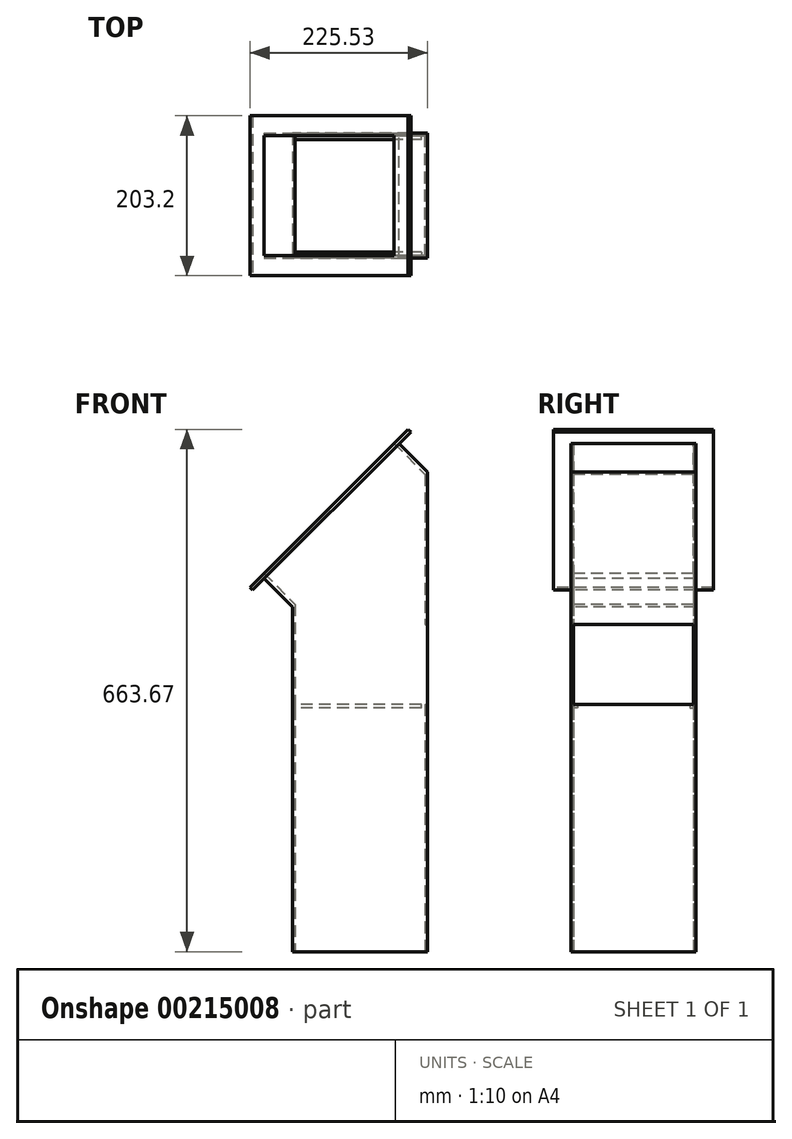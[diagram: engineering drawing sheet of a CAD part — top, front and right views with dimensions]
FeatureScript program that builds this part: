
annotation { "Feature Type Name" : "Feature", "Feature Type Description" : "" }
export const myFeature = defineFeature(function(context is Context, id is Id, definition is map)
    precondition{}
    {
        {
            var Q0;
            Q0=qCreatedBy(makeId("Top.planeOp"),FACE);
            var sketch = newSketch(context, id + "F0", { "sketchPlane" : qUnion([Q0])});
            skLineSegment(sketch, "E0.bottom", {"start": v(82.55, -76.2) * mm, "end": v(-82.55, -76.2) * mm});
            skLineSegment(sketch, "E0.top", {"start": v(82.55, 76.2) * mm, "end": v(-82.55, 76.2) * mm});
            skLineSegment(sketch, "E0.left", {"start": v(82.55, -76.2) * mm, "end": v(82.55, 76.2) * mm});
            skLineSegment(sketch, "E0.right", {"start": v(-82.55, -76.2) * mm, "end": v(-82.55, 76.2) * mm});
            skPoint(sketch, "E0.middle", {"position": v(0, 0) * mm});
            skLineSegment(sketch, "E1.0", {"start": v(-85.73, -79.38) * mm, "end": v(-85.73, 79.37) * mm});
            skLineSegment(sketch, "E1.1", {"start": v(85.73, -79.37) * mm, "end": v(-85.73, -79.38) * mm});
            skLineSegment(sketch, "E1.2", {"start": v(85.73, -79.37) * mm, "end": v(85.72, 79.38) * mm});
            skLineSegment(sketch, "E1.3", {"start": v(85.72, 79.38) * mm, "end": v(-85.73, 79.37) * mm});
            skSolve(sketch);
        }
        {
            var Q0;
            Q0 = qSketchRegion(id + "F0", true);
            extrude(context, id + "F1", {"entities" : qUnion([Q0]), "depth" : 609.6 * mm});
        }
        {
            var Q0;
            Q0=makeQuery(id+"F1.opExtrude","SWEPT_FACE",FACE,{"disambiguationData":[OSD([sQuery(id+"F0.wireOp",EDGE,"E1.1")])]});
            var sketch = newSketch(context, id + "F2", { "sketchPlane" : qUnion([Q0])});
            skLineSegment(sketch, "E2", {"start": v(85.72, 609.6) * mm, "end": v(-85.73, 609.6) * mm});
            skLineSegment(sketch, "E3", {"start": v(-85.73, 609.6) * mm, "end": v(-85.73, 438.15) * mm});
            skLineSegment(sketch, "E4", {"start": v(-85.73, 438.15) * mm, "end": v(85.72, 609.6) * mm});
            skSolve(sketch);
        }
        {
            var Q0;
            Q0 = qSketchRegion(id + "F2", true);
            extrude(context, id + "F3", {"entities" : qUnion([Q0]), "operationType" : NewBodyOperationType.REMOVE, "endBound" : BoundingType.THROUGH_ALL, "oppositeDirection" : true, "depth" : 25.4 * mm});
        }
        {
            var Q0;
            Q0=makeQuery(id+"F3.boolean.opBoolean","COPY",FACE,{"derivedFrom":makeQuery(id+"F3.opExtrude","SWEPT_FACE",FACE,{"disambiguationData":[OSD([sQuery(id+"F2.wireOp",EDGE,"E4")])]})});
            var sketch = newSketch(context, id + "F4", { "sketchPlane" : qUnion([Q0])});
            skLineSegment(sketch, "E5.0", {"start": v(-76.2, 253.7) * mm, "end": v(-76.2, 487.18) * mm});
            skLineSegment(sketch, "E6.0", {"start": v(-76.2, 487.18) * mm, "end": v(76.2, 487.18) * mm});
            skLineSegment(sketch, "E7.0", {"start": v(76.2, 253.7) * mm, "end": v(76.2, 487.18) * mm});
            skLineSegment(sketch, "E8.0", {"start": v(-76.2, 253.7) * mm, "end": v(76.2, 253.7) * mm});
            skLineSegment(sketch, "E9.0", {"start": v(-101.6, 228.3) * mm, "end": v(-101.6, 512.58) * mm});
            skLineSegment(sketch, "E9.1", {"start": v(-101.6, 228.3) * mm, "end": v(101.6, 228.3) * mm});
            skLineSegment(sketch, "E9.2", {"start": v(101.6, 228.3) * mm, "end": v(101.6, 512.58) * mm});
            skLineSegment(sketch, "E9.3", {"start": v(-101.6, 512.58) * mm, "end": v(101.6, 512.58) * mm});
            skSolve(sketch);
        }
        {
            var Q0;
            Q0 = qSketchRegion(id + "F4", true);
            extrude(context, id + "F5", {"entities" : qUnion([Q0]), "operationType" : NewBodyOperationType.ADD, "depth" : 55.56 * mm});
        }
        {
            var Q0;
            Q0=makeQuery(id+"F1.opExtrude","SWEPT_FACE",FACE,{"disambiguationData":[OSD([sQuery(id+"F0.wireOp",EDGE,"E1.2")])]});
            var sketch = newSketch(context, id + "F6", { "sketchPlane" : qUnion([Q0])});
            skLineSegment(sketch, "E10.0", {"start": v(76.2, 441.32) * mm, "end": v(-76.2, 441.32) * mm, "construction": true});
            skLineSegment(sketch, "E11.0", {"start": v(76.2, 415.93) * mm, "end": v(-76.2, 415.93) * mm});
            skLineSegment(sketch, "E12", {"start": v(-76.2, 415.93) * mm, "end": v(-76.2, 314.32) * mm});
            skLineSegment(sketch, "E13", {"start": v(-76.2, 314.32) * mm, "end": v(76.2, 314.32) * mm});
            skLineSegment(sketch, "E14", {"start": v(76.2, 314.32) * mm, "end": v(76.2, 415.93) * mm});
            skSolve(sketch);
        }
        {
            var Q0;
            Q0 = qSketchRegion(id + "F6", true);
            extrude(context, id + "F7", {"entities" : qUnion([Q0]), "operationType" : NewBodyOperationType.REMOVE, "oppositeDirection" : true, "depth" : 25.4 * mm});
        }
        {
            var Q0;
            Q0=makeQuery(id+"F7.boolean.opBoolean","MERGE",FACE,{"derivedFrom":[makeQuery(id+"F5.boolean.opBoolean","MERGE",FACE,{"derivedFrom":[makeQuery(id+"F1.opExtrude","SWEPT_FACE",FACE,{"disambiguationData":[OSD([sQuery(id+"F0.wireOp",EDGE,"E0.bottom")])]}),makeQuery(id+"F5.opExtrude","SWEPT_FACE",FACE,{"disambiguationData":[OSD([sQuery(id+"F4.wireOp",EDGE,"E7.0")])]})]}),makeQuery(id+"F7.opExtrude","SWEPT_FACE",FACE,{"disambiguationData":[OSD([sQuery(id+"F6.wireOp",EDGE,"E12")])]})]});
            var sketch = newSketch(context, id + "F8", { "sketchPlane" : qUnion([Q0])});
            skLineSegment(sketch, "E15.0", {"start": v(-82.55, 314.32) * mm, "end": v(-85.72, 314.32) * mm});
            skLineSegment(sketch, "E16.bottom", {"start": v(-82.55, 314.32) * mm, "end": v(82.55, 314.32) * mm});
            skLineSegment(sketch, "E16.top", {"start": v(-82.55, 309.56) * mm, "end": v(82.55, 309.56) * mm});
            skLineSegment(sketch, "E16.left", {"start": v(-82.55, 314.32) * mm, "end": v(-82.55, 309.56) * mm});
            skLineSegment(sketch, "E16.right", {"start": v(82.55, 314.32) * mm, "end": v(82.55, 309.56) * mm});
            skLineSegment(sketch, "E17", {"start": v(-77.79, 314.32) * mm, "end": v(-77.79, 309.56) * mm});
            skSolve(sketch);
        }
        {
            var Q0;
            {var subQ0=sQuery(id+"F8.wireOp",EDGE,"E16.right");Q0=makeQuery(id+"F8.imprint","IMPRINT",FACE,{"disambiguationData":[TD([[makeQuery(id+"F8.imprint","IMPRINT",EDGE,{"derivedFrom":subQ0}),-1.0]])]});}
            extrude(context, id + "F9", {"entities" : qUnion([Q0]), "operationType" : NewBodyOperationType.ADD, "depth" : 4.76 * mm});
        }
        {
            var Q0;
            Q0=makeQuery(id+"F7.boolean.opBoolean","MERGE",FACE,{"derivedFrom":[makeQuery(id+"F5.boolean.opBoolean","MERGE",FACE,{"derivedFrom":[makeQuery(id+"F1.opExtrude","SWEPT_FACE",FACE,{"disambiguationData":[OSD([sQuery(id+"F0.wireOp",EDGE,"E0.top")])]}),makeQuery(id+"F5.opExtrude","SWEPT_FACE",FACE,{"disambiguationData":[OSD([sQuery(id+"F4.wireOp",EDGE,"E5.0")])]})]}),makeQuery(id+"F7.opExtrude","SWEPT_FACE",FACE,{"disambiguationData":[OSD([sQuery(id+"F6.wireOp",EDGE,"E14")])]})]});
            var sketch = newSketch(context, id + "F10", { "sketchPlane" : qUnion([Q0])});
            skLineSegment(sketch, "E18.0", {"start": v(82.55, 314.32) * mm, "end": v(85.72, 314.32) * mm});
            skLineSegment(sketch, "E19.bottom", {"start": v(82.55, 314.32) * mm, "end": v(-82.55, 314.32) * mm});
            skLineSegment(sketch, "E19.top", {"start": v(82.55, 309.56) * mm, "end": v(-82.55, 309.56) * mm});
            skLineSegment(sketch, "E19.left", {"start": v(82.55, 314.32) * mm, "end": v(82.55, 309.56) * mm});
            skLineSegment(sketch, "E19.right", {"start": v(-82.55, 314.32) * mm, "end": v(-82.55, 309.56) * mm});
            skLineSegment(sketch, "E20", {"start": v(77.79, 309.56) * mm, "end": v(77.79, 314.32) * mm});
            skPoint(sketch, "E20.endSnap0", {"position": v(84.14, 314.32) * mm});
            skSolve(sketch);
        }
        {
            var Q0;
            {var subQ0=sQuery(id+"F10.wireOp",EDGE,"E19.right");Q0=makeQuery(id+"F10.imprint","IMPRINT",FACE,{"disambiguationData":[TD([[makeQuery(id+"F10.imprint","IMPRINT",EDGE,{"derivedFrom":subQ0}),1.0]])]});}
            extrude(context, id + "F11", {"entities" : qUnion([Q0]), "operationType" : NewBodyOperationType.ADD, "depth" : 4.76 * mm});
        }
        {
            var Q0;
            Q0=makeQuery(id+"F4.imprint","IMPRINT",FACE,{"disambiguationData":[TD([[makeQuery(id+"F4.imprint","IMPRINT",EDGE,{"derivedFrom":sQuery(id+"F4.wireOp",EDGE,"E9.0")}),-1.0]])]});
            var sketch = newSketch(context, id + "F12", { "sketchPlane" : qUnion([Q0])});
            skLineSegment(sketch, "E21.0", {"start": v(-101.6, 512.58) * mm, "end": v(101.6, 512.58) * mm});
            skLineSegment(sketch, "E22.0", {"start": v(101.6, 228.3) * mm, "end": v(101.6, 512.58) * mm});
            skLineSegment(sketch, "E23.0", {"start": v(79.37, 491.67) * mm, "end": v(-79.38, 491.67) * mm});
            skLineSegment(sketch, "E24.0", {"start": v(79.37, 249.2) * mm, "end": v(79.37, 491.67) * mm});
            skLineSegment(sketch, "E25.0", {"start": v(-79.38, 491.67) * mm, "end": v(-79.38, 60.62) * mm});
            skLineSegment(sketch, "E26.0", {"start": v(-101.6, 228.3) * mm, "end": v(-101.6, 512.58) * mm});
            skLineSegment(sketch, "E27.0", {"start": v(-101.6, 228.3) * mm, "end": v(101.6, 228.3) * mm});
            skLineSegment(sketch, "E28.0", {"start": v(-79.37, 249.2) * mm, "end": v(79.37, 249.2) * mm});
            skSolve(sketch);
        }
        {
            var Q0;
            Q0 = qSketchRegion(id + "F12", true);
            extrude(context, id + "F13", {"entities" : qUnion([Q0]), "operationType" : NewBodyOperationType.REMOVE, "depth" : 50.8 * mm});
        }
    });
